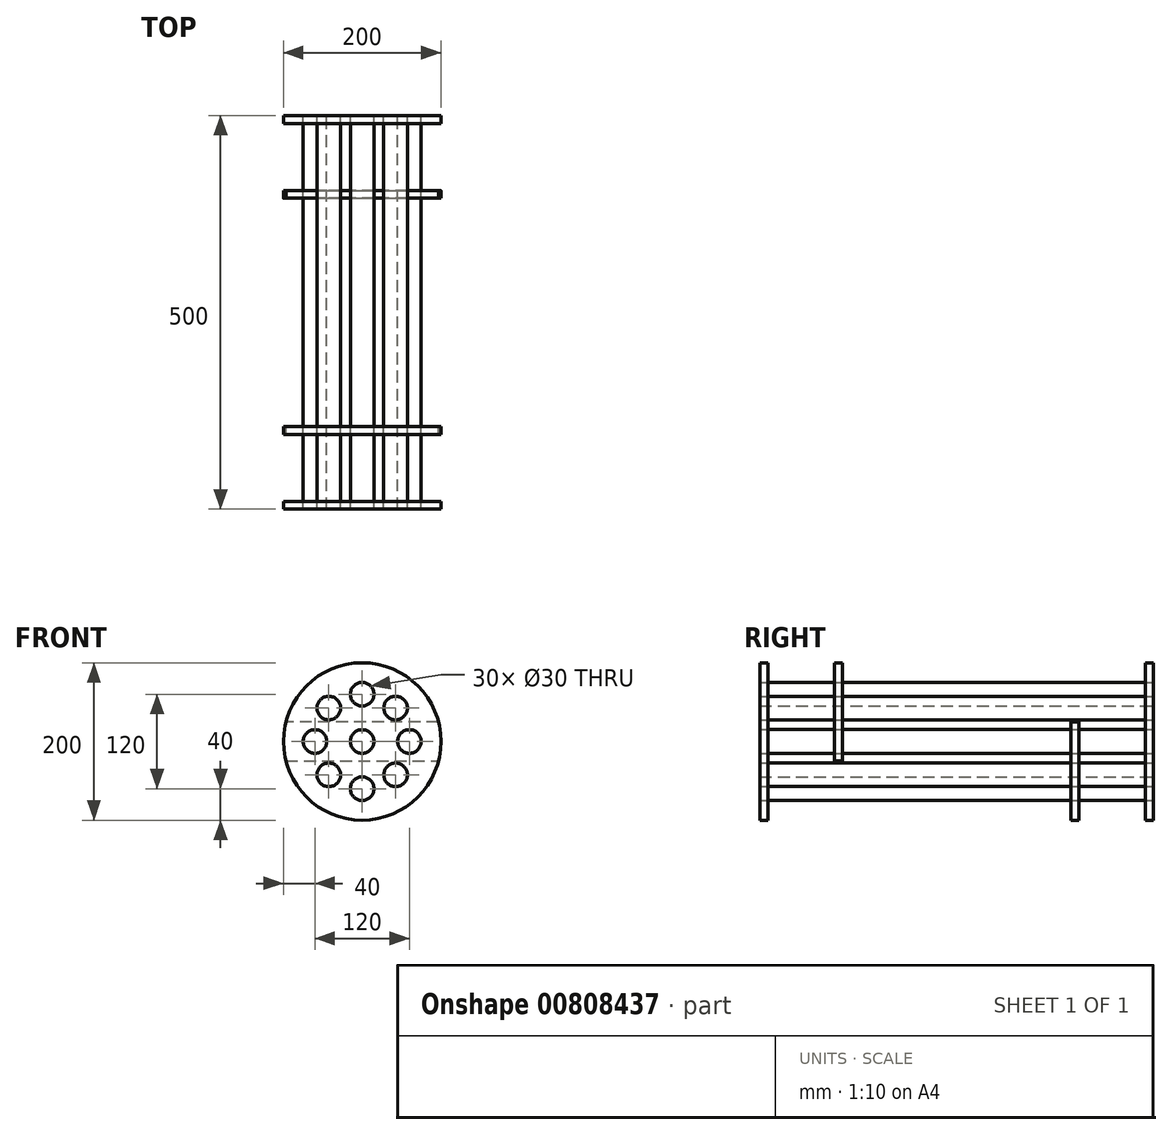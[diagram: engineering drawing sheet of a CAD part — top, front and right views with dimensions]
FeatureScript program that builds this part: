
annotation { "Feature Type Name" : "Feature", "Feature Type Description" : "" }
export const myFeature = defineFeature(function(context is Context, id is Id, definition is map)
    precondition{}
    {
        {
            var Q0;
            Q0=qCreatedBy(makeId("Right.planeOp"),FACE);
            var sketch = newSketch(context, id + "F0", { "sketchPlane" : qUnion([Q0])});
            skPoint(sketch, "E0.middle", {"position": v(0, 0) * mm});
            skLineSegment(sketch, "E1", {"start": v(0, 0) * mm, "end": v(-300, 0) * mm});
            skLineSegment(sketch, "E2", {"start": v(-300, 0) * mm, "end": v(-300, 50) * mm});
            skLineSegment(sketch, "E3", {"start": v(-250, 100) * mm, "end": v(250, 100) * mm});
            skLineSegment(sketch, "E4", {"start": v(300, 50) * mm, "end": v(300, 0) * mm});
            skLineSegment(sketch, "E5", {"start": v(300, 0) * mm, "end": v(0, 0) * mm});
            skPoint(sketch, "E6.visualSharp", {"position": v(-300, 100) * mm});
            skArc(sketch, "E6.filletArc", {"start": v(-250, 100) * mm, "mid": v(-285.36, 85.36) * mm, "end": v(-300, 50) * mm});
            skPoint(sketch, "E7.visualSharp", {"position": v(300, 100) * mm});
            skArc(sketch, "E7.filletArc", {"start": v(300, 50) * mm, "mid": v(285.36, 85.36) * mm, "end": v(250, 100) * mm});
            skLineSegment(sketch, "E8.bottom", {"start": v(-300, 0) * mm, "end": v(-300, 0) * mm});
            skLineSegment(sketch, "E8.top", {"start": v(-300, 50) * mm, "end": v(-300, 50) * mm});
            skLineSegment(sketch, "E9.bottom", {"start": v(-300, 0) * mm, "end": v(-350, 0) * mm});
            skLineSegment(sketch, "E9.top", {"start": v(-300, 50) * mm, "end": v(-350, 50) * mm});
            skLineSegment(sketch, "E9.right", {"start": v(-350, 0) * mm, "end": v(-350, 50) * mm});
            skLineSegment(sketch, "E10.bottom", {"start": v(300, 0) * mm, "end": v(350, 0) * mm});
            skLineSegment(sketch, "E10.top", {"start": v(300, 50) * mm, "end": v(350, 50) * mm});
            skLineSegment(sketch, "E10.left", {"start": v(300, 0) * mm, "end": v(300, 50) * mm});
            skLineSegment(sketch, "E10.right", {"start": v(350, 0) * mm, "end": v(350, 50) * mm});
            skLineSegment(sketch, "E11", {"start": v(-378.43, 0) * mm, "end": v(537.44, 0) * mm, "construction": true});
            skSolve(sketch);
        }
        {
            var Q0;
            Q0=qCreatedBy(makeId("Front.planeOp"),FACE);
            var sketch = newSketch(context, id + "F1", { "sketchPlane" : qUnion([Q0])});
            skCircle(sketch, "E12", {"center": v(0, 0) * mm, "radius": 100 * mm, "construction": true});
            skCircle(sketch, "E13", {"center": v(0, 0) * mm, "radius": 15 * mm});
            skCircle(sketch, "E14", {"center": v(60, 0) * mm, "radius": 15 * mm});
            skCircle(sketch, "E15", {"center": v(-60, 0) * mm, "radius": 15 * mm});
            skCircle(sketch, "E16", {"center": v(42.43, -42.43) * mm, "radius": 15 * mm});
            skCircle(sketch, "E17", {"center": v(42.43, 42.43) * mm, "radius": 15 * mm});
            skCircle(sketch, "E18", {"center": v(-42.43, -42.43) * mm, "radius": 15 * mm});
            skCircle(sketch, "E19", {"center": v(-42.43, 42.43) * mm, "radius": 15 * mm});
            skCircle(sketch, "E20", {"center": v(0, -60) * mm, "radius": 15 * mm});
            skCircle(sketch, "E21", {"center": v(0, 60) * mm, "radius": 15 * mm});
            skLineSegment(sketch, "E22", {"start": v(42.43, 42.43) * mm, "end": v(0, 0) * mm, "construction": true});
            skLineSegment(sketch, "E23", {"start": v(42.43, -42.43) * mm, "end": v(0, 0) * mm, "construction": true});
            skLineSegment(sketch, "E24", {"start": v(-42.43, -42.43) * mm, "end": v(0, 0) * mm, "construction": true});
            skLineSegment(sketch, "E25", {"start": v(-42.43, 42.43) * mm, "end": v(0, 0) * mm, "construction": true});
            skSolve(sketch);
        }
        {
            var Q0;
            Q0=makeQuery(id+"F1.imprint","IMPRINT",FACE,{"disambiguationData":[TD([[makeQuery(id+"F1.imprint","IMPRINT",EDGE,{"derivedFrom":sQuery(id+"F1.wireOp",EDGE,"E17")}),1.0]])]});
            var Q1;
            Q1=makeQuery(id+"F1.imprint","IMPRINT",FACE,{"disambiguationData":[TD([[makeQuery(id+"F1.imprint","IMPRINT",EDGE,{"derivedFrom":sQuery(id+"F1.wireOp",EDGE,"E19")}),1.0]])]});
            var Q2;
            Q2=makeQuery(id+"F1.imprint","IMPRINT",FACE,{"disambiguationData":[TD([[makeQuery(id+"F1.imprint","IMPRINT",EDGE,{"derivedFrom":sQuery(id+"F1.wireOp",EDGE,"E13")}),1.0]])]});
            var Q3;
            Q3=makeQuery(id+"F1.imprint","IMPRINT",FACE,{"disambiguationData":[TD([[makeQuery(id+"F1.imprint","IMPRINT",EDGE,{"derivedFrom":sQuery(id+"F1.wireOp",EDGE,"E15")}),1.0]])]});
            var Q4;
            Q4=makeQuery(id+"F1.imprint","IMPRINT",FACE,{"disambiguationData":[TD([[makeQuery(id+"F1.imprint","IMPRINT",EDGE,{"derivedFrom":sQuery(id+"F1.wireOp",EDGE,"E18")}),1.0]])]});
            var Q5;
            Q5=makeQuery(id+"F1.imprint","IMPRINT",FACE,{"disambiguationData":[TD([[makeQuery(id+"F1.imprint","IMPRINT",EDGE,{"derivedFrom":sQuery(id+"F1.wireOp",EDGE,"E16")}),1.0]])]});
            var Q6;
            Q6=makeQuery(id+"F1.imprint","IMPRINT",FACE,{"disambiguationData":[TD([[makeQuery(id+"F1.imprint","IMPRINT",EDGE,{"derivedFrom":sQuery(id+"F1.wireOp",EDGE,"E14")}),1.0]])]});
            var Q7;
            Q7=makeQuery(id+"F1.imprint","IMPRINT",FACE,{"disambiguationData":[TD([[makeQuery(id+"F1.imprint","IMPRINT",EDGE,{"derivedFrom":sQuery(id+"F1.wireOp",EDGE,"E21")}),1.0]])]});
            var Q8;
            Q8=makeQuery(id+"F1.imprint","IMPRINT",FACE,{"disambiguationData":[TD([[makeQuery(id+"F1.imprint","IMPRINT",EDGE,{"derivedFrom":sQuery(id+"F1.wireOp",EDGE,"E20")}),1.0]])]});
            extrude(context, id + "F2", {"entities" : qUnion([Q0, Q1, Q2, Q3, Q4, Q5, Q6, Q7, Q8]), "endBound" : BoundingType.SYMMETRIC, "depth" : 500 * mm, "offsetDistance" : 25 * mm});
        }
        {
            var Q0;
            Q0=makeQuery(id+"F2.opExtrude","CAP_FACE",FACE,{"disambiguationData":[OSD([sQuery(id+"F1.wireOp",EDGE,"E19")])],"isStart":true});
            var sketch = newSketch(context, id + "F3", { "sketchPlane" : qUnion([Q0])});
            skCircle(sketch, "E26", {"center": v(0, 0) * mm, "radius": 100 * mm});
            skSolve(sketch);
        }
        {
            var Q0;
            Q0=makeQuery(id+"F3.imprint","IMPRINT",FACE,{"disambiguationData":[TD([[makeQuery(id+"F3.imprint","IMPRINT",EDGE,{"derivedFrom":sQuery(id+"F3.wireOp",EDGE,"E26")}),1.0]])]});
            extrude(context, id + "F4", {"entities" : qUnion([Q0]), "oppositeDirection" : true, "depth" : 10 * mm, "offsetDistance" : 25 * mm});
        }
        {
            var Q0;
            Q0=makeQuery(id+"F2.opExtrude","SWEPT_BODY",BODY,{"disambiguationData":[OSD([sQuery(id+"F1.wireOp",EDGE,"E20")])]});
            var Q1;
            Q1=makeQuery(id+"F2.opExtrude","SWEPT_BODY",BODY,{"disambiguationData":[OSD([sQuery(id+"F1.wireOp",EDGE,"E18")])]});
            var Q2;
            Q2=makeQuery(id+"F2.opExtrude","SWEPT_BODY",BODY,{"disambiguationData":[OSD([sQuery(id+"F1.wireOp",EDGE,"E15")])]});
            var Q3;
            Q3=makeQuery(id+"F2.opExtrude","SWEPT_BODY",BODY,{"disambiguationData":[OSD([sQuery(id+"F1.wireOp",EDGE,"E19")])]});
            var Q4;
            Q4=makeQuery(id+"F2.opExtrude","SWEPT_BODY",BODY,{"disambiguationData":[OSD([sQuery(id+"F1.wireOp",EDGE,"E21")])]});
            var Q5;
            Q5=makeQuery(id+"F2.opExtrude","SWEPT_BODY",BODY,{"disambiguationData":[OSD([sQuery(id+"F1.wireOp",EDGE,"E17")])]});
            var Q6;
            Q6=makeQuery(id+"F2.opExtrude","SWEPT_BODY",BODY,{"disambiguationData":[OSD([sQuery(id+"F1.wireOp",EDGE,"E14")])]});
            var Q7;
            Q7=makeQuery(id+"F2.opExtrude","SWEPT_BODY",BODY,{"disambiguationData":[OSD([sQuery(id+"F1.wireOp",EDGE,"E16")])]});
            var Q8;
            Q8=makeQuery(id+"F2.opExtrude","SWEPT_BODY",BODY,{"disambiguationData":[OSD([sQuery(id+"F1.wireOp",EDGE,"E13")])]});
            var Q9;
            Q9=makeQuery(id+"F4.opExtrude","SWEPT_BODY",BODY,{"disambiguationData":[OSD([sQuery(id+"F1.wireOp",EDGE,"E19"),sQuery(id+"F3.wireOp",EDGE,"E26")])]});
            booleanBodies(context, id + "F5", {"operationType" : BooleanOperationType.SUBTRACTION, "tools" : qUnion([Q0, Q1, Q2, Q3, Q4, Q5, Q6, Q7, Q8]), "targets" : qUnion([Q9]), "keepTools" : true});
        }
        {
            var Q0;
            Q0=makeQuery(id+"F2.opExtrude","CAP_FACE",FACE,{"disambiguationData":[OSD([sQuery(id+"F1.wireOp",EDGE,"E15")])],"isStart":false});
            var sketch = newSketch(context, id + "F6", { "sketchPlane" : qUnion([Q0])});
            skCircle(sketch, "E27", {"center": v(0, 0) * mm, "radius": 100 * mm});
            skSolve(sketch);
        }
        {
            var Q0;
            Q0=qSketchRegion(id+"F6",true);
            extrude(context, id + "F7", {"entities" : qUnion([Q0]), "oppositeDirection" : true, "depth" : 10 * mm, "offsetDistance" : 25 * mm});
        }
        {
            var Q0;
            Q0=makeQuery(id+"F2.opExtrude","SWEPT_BODY",BODY,{"disambiguationData":[OSD([sQuery(id+"F1.wireOp",EDGE,"E19")])]});
            var Q1;
            Q1=makeQuery(id+"F2.opExtrude","SWEPT_BODY",BODY,{"disambiguationData":[OSD([sQuery(id+"F1.wireOp",EDGE,"E15")])]});
            var Q2;
            Q2=makeQuery(id+"F2.opExtrude","SWEPT_BODY",BODY,{"disambiguationData":[OSD([sQuery(id+"F1.wireOp",EDGE,"E18")])]});
            var Q3;
            Q3=makeQuery(id+"F2.opExtrude","SWEPT_BODY",BODY,{"disambiguationData":[OSD([sQuery(id+"F1.wireOp",EDGE,"E20")])]});
            var Q4;
            Q4=makeQuery(id+"F2.opExtrude","SWEPT_BODY",BODY,{"disambiguationData":[OSD([sQuery(id+"F1.wireOp",EDGE,"E16")])]});
            var Q5;
            Q5=makeQuery(id+"F2.opExtrude","SWEPT_BODY",BODY,{"disambiguationData":[OSD([sQuery(id+"F1.wireOp",EDGE,"E14")])]});
            var Q6;
            Q6=makeQuery(id+"F2.opExtrude","SWEPT_BODY",BODY,{"disambiguationData":[OSD([sQuery(id+"F1.wireOp",EDGE,"E17")])]});
            var Q7;
            Q7=makeQuery(id+"F2.opExtrude","SWEPT_BODY",BODY,{"disambiguationData":[OSD([sQuery(id+"F1.wireOp",EDGE,"E21")])]});
            var Q8;
            Q8=makeQuery(id+"F2.opExtrude","SWEPT_BODY",BODY,{"disambiguationData":[OSD([sQuery(id+"F1.wireOp",EDGE,"E13")])]});
            var Q9;
            Q9=makeQuery(id+"F7.opExtrude","SWEPT_BODY",BODY,{"disambiguationData":[OSD([sQuery(id+"F6.wireOp",EDGE,"E27")])]});
            booleanBodies(context, id + "F8", {"operationType" : BooleanOperationType.SUBTRACTION, "tools" : qUnion([Q0, Q1, Q2, Q3, Q4, Q5, Q6, Q7, Q8]), "targets" : qUnion([Q9]), "keepTools" : true});
        }
        {
            var Q0;
            Q0=qCreatedBy(makeId("Front.planeOp"),FACE);
            cPlane(context, id + "F9", {"entities" : qUnion([Q0]), "cplaneType" : CPlaneType.OFFSET, "offset" : 150 * mm, "width" : 150 * mm, "height" : 150 * mm});
        }
        {
            var Q0;
            Q0=qCreatedBy(makeId("Front.planeOp"),FACE);
            cPlane(context, id + "F10", {"entities" : qUnion([Q0]), "cplaneType" : CPlaneType.OFFSET, "offset" : 150 * mm, "oppositeDirection" : true, "width" : 150 * mm, "height" : 150 * mm});
        }
        {
            var Q0;
            Q0=qCreatedBy(id+"F9.planeOp",FACE);
            var sketch = newSketch(context, id + "F11", { "sketchPlane" : qUnion([Q0])});
            skCircle(sketch, "E28", {"center": v(0, 0) * mm, "radius": 100 * mm});
            skLineSegment(sketch, "E29", {"start": v(-96.82, -25) * mm, "end": v(96.82, -25) * mm});
            skSolve(sketch);
        }
        {
            var Q0;
            {var subQ0=sQuery(id+"F11.wireOp",EDGE,"E29");Q0=makeQuery(id+"F11.imprint","IMPRINT",FACE,{"disambiguationData":[TD([[makeQuery(id+"F11.imprint","IMPRINT",EDGE,{"derivedFrom":subQ0}),1.0]])]});}
            extrude(context, id + "F12", {"entities" : qUnion([Q0]), "endBound" : BoundingType.SYMMETRIC, "depth" : 10 * mm, "offsetDistance" : 25 * mm});
        }
        {
            var Q0;
            Q0=makeQuery(id+"F2.opExtrude","SWEPT_BODY",BODY,{"disambiguationData":[OSD([sQuery(id+"F1.wireOp",EDGE,"E19")])]});
            var Q1;
            Q1=makeQuery(id+"F2.opExtrude","SWEPT_BODY",BODY,{"disambiguationData":[OSD([sQuery(id+"F1.wireOp",EDGE,"E21")])]});
            var Q2;
            Q2=makeQuery(id+"F2.opExtrude","SWEPT_BODY",BODY,{"disambiguationData":[OSD([sQuery(id+"F1.wireOp",EDGE,"E17")])]});
            var Q3;
            Q3=makeQuery(id+"F2.opExtrude","SWEPT_BODY",BODY,{"disambiguationData":[OSD([sQuery(id+"F1.wireOp",EDGE,"E14")])]});
            var Q4;
            Q4=makeQuery(id+"F2.opExtrude","SWEPT_BODY",BODY,{"disambiguationData":[OSD([sQuery(id+"F1.wireOp",EDGE,"E20")])]});
            var Q5;
            Q5=makeQuery(id+"F2.opExtrude","SWEPT_BODY",BODY,{"disambiguationData":[OSD([sQuery(id+"F1.wireOp",EDGE,"E18")])]});
            var Q6;
            Q6=makeQuery(id+"F2.opExtrude","SWEPT_BODY",BODY,{"disambiguationData":[OSD([sQuery(id+"F1.wireOp",EDGE,"E15")])]});
            var Q7;
            Q7=makeQuery(id+"F2.opExtrude","SWEPT_BODY",BODY,{"disambiguationData":[OSD([sQuery(id+"F1.wireOp",EDGE,"E13")])]});
            var Q8;
            Q8=makeQuery(id+"F12.opExtrude","SWEPT_BODY",BODY,{"disambiguationData":[OSD([sQuery(id+"F11.wireOp",EDGE,"E28"),sQuery(id+"F11.wireOp",EDGE,"E29")])]});
            booleanBodies(context, id + "F13", {"operationType" : BooleanOperationType.SUBTRACTION, "tools" : qUnion([Q0, Q1, Q2, Q3, Q4, Q5, Q6, Q7]), "targets" : qUnion([Q8]), "keepTools" : true});
        }
        {
            var Q0;
            Q0=qCreatedBy(id+"F10.planeOp",FACE);
            var sketch = newSketch(context, id + "F14", { "sketchPlane" : qUnion([Q0])});
            skCircle(sketch, "E30", {"center": v(0, 0) * mm, "radius": 100 * mm});
            skLineSegment(sketch, "E31", {"start": v(96.82, 25) * mm, "end": v(-96.82, 25) * mm});
            skSolve(sketch);
        }
        {
            var Q0;
            {var subQ0=sQuery(id+"F14.wireOp",EDGE,"E31");Q0=makeQuery(id+"F14.imprint","IMPRINT",FACE,{"disambiguationData":[TD([[makeQuery(id+"F14.imprint","IMPRINT",EDGE,{"derivedFrom":subQ0}),1.0]])]});}
            extrude(context, id + "F15", {"entities" : qUnion([Q0]), "endBound" : BoundingType.SYMMETRIC, "depth" : 10 * mm, "offsetDistance" : 25 * mm});
        }
        {
            var Q0;
            Q0=makeQuery(id+"F2.opExtrude","SWEPT_BODY",BODY,{"disambiguationData":[OSD([sQuery(id+"F1.wireOp",EDGE,"E17")])]});
            var Q1;
            Q1=makeQuery(id+"F2.opExtrude","SWEPT_BODY",BODY,{"disambiguationData":[OSD([sQuery(id+"F1.wireOp",EDGE,"E14")])]});
            var Q2;
            Q2=makeQuery(id+"F2.opExtrude","SWEPT_BODY",BODY,{"disambiguationData":[OSD([sQuery(id+"F1.wireOp",EDGE,"E16")])]});
            var Q3;
            Q3=makeQuery(id+"F2.opExtrude","SWEPT_BODY",BODY,{"disambiguationData":[OSD([sQuery(id+"F1.wireOp",EDGE,"E20")])]});
            var Q4;
            Q4=makeQuery(id+"F2.opExtrude","SWEPT_BODY",BODY,{"disambiguationData":[OSD([sQuery(id+"F1.wireOp",EDGE,"E18")])]});
            var Q5;
            Q5=makeQuery(id+"F2.opExtrude","SWEPT_BODY",BODY,{"disambiguationData":[OSD([sQuery(id+"F1.wireOp",EDGE,"E15")])]});
            var Q6;
            Q6=makeQuery(id+"F2.opExtrude","SWEPT_BODY",BODY,{"disambiguationData":[OSD([sQuery(id+"F1.wireOp",EDGE,"E13")])]});
            var Q7;
            Q7=makeQuery(id+"F2.opExtrude","SWEPT_BODY",BODY,{"disambiguationData":[OSD([sQuery(id+"F1.wireOp",EDGE,"E19")])]});
            var Q8;
            Q8=makeQuery(id+"F2.opExtrude","SWEPT_BODY",BODY,{"disambiguationData":[OSD([sQuery(id+"F1.wireOp",EDGE,"E21")])]});
            var Q9;
            Q9=makeQuery(id+"F15.opExtrude","SWEPT_BODY",BODY,{"disambiguationData":[OSD([sQuery(id+"F14.wireOp",EDGE,"E30"),sQuery(id+"F14.wireOp",EDGE,"E31")])]});
            booleanBodies(context, id + "F16", {"operationType" : BooleanOperationType.SUBTRACTION, "tools" : qUnion([Q0, Q1, Q2, Q3, Q4, Q5, Q6, Q7, Q8]), "targets" : qUnion([Q9]), "keepTools" : true});
        }
    });
